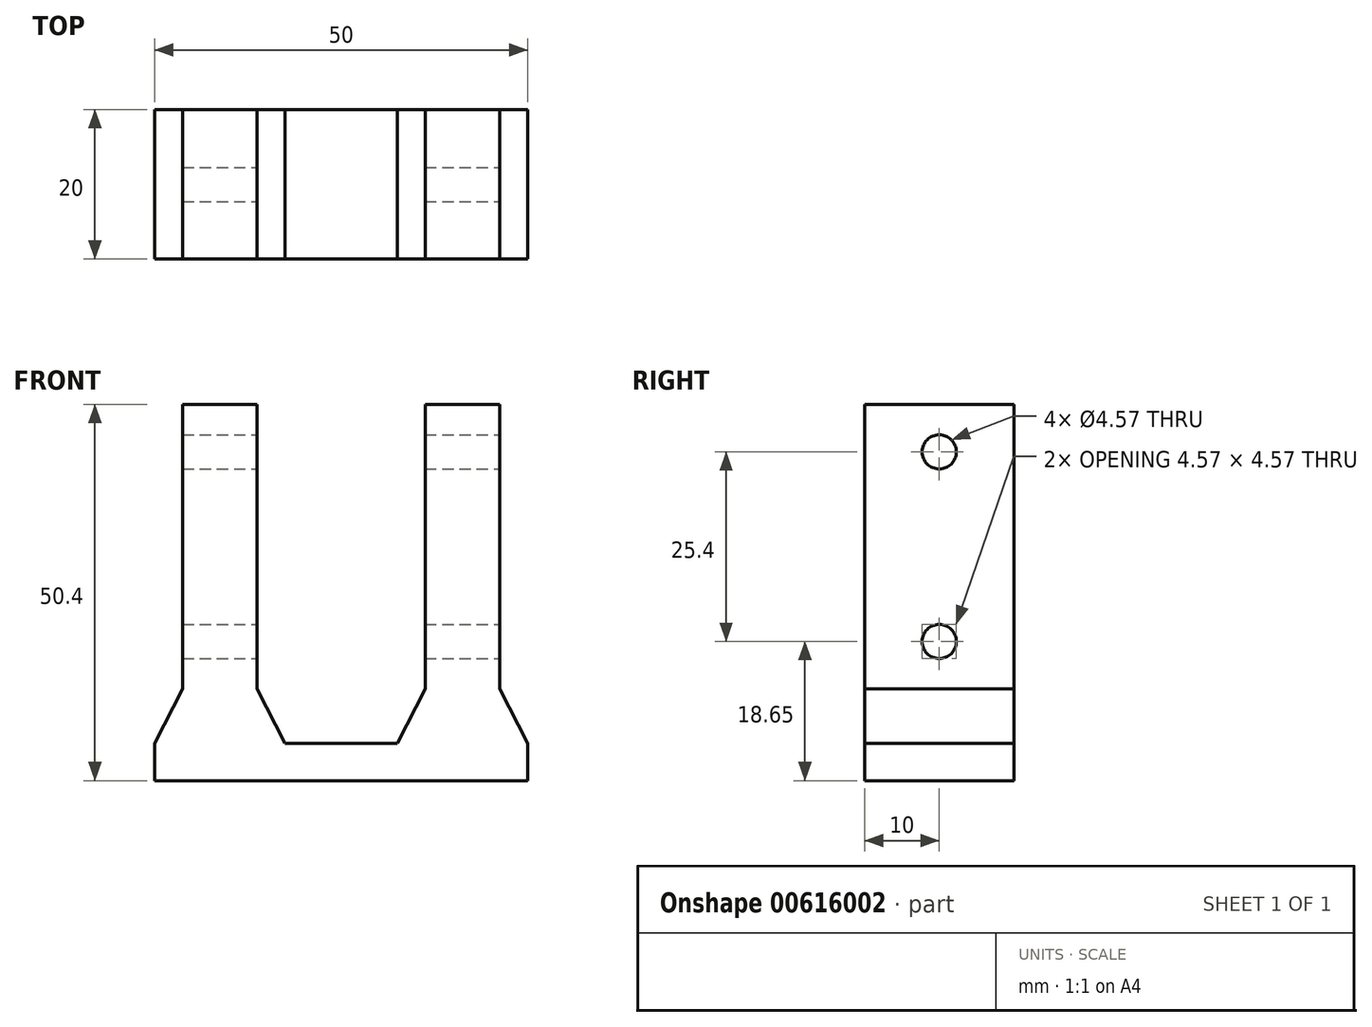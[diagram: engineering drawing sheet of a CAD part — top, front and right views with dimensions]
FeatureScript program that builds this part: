
annotation { "Feature Type Name" : "Feature", "Feature Type Description" : "" }
export const myFeature = defineFeature(function(context is Context, id is Id, definition is map)
    precondition{}
    {
        {
            var Q0;
            Q0=qCreatedBy(makeId("Top.planeOp"),FACE);
            var sketch = newSketch(context, id + "F0", { "sketchPlane" : qUnion([Q0])});
            skLineSegment(sketch, "E0.bottom", {"start": v(25, 10) * mm, "end": v(-25, 10) * mm});
            skLineSegment(sketch, "E0.top", {"start": v(25, -10) * mm, "end": v(-25, -10) * mm});
            skLineSegment(sketch, "E0.left", {"start": v(25, 10) * mm, "end": v(25, -10) * mm});
            skLineSegment(sketch, "E0.right", {"start": v(-25, 10) * mm, "end": v(-25, -10) * mm});
            skPoint(sketch, "E0.middle", {"position": v(0, 0) * mm});
            skSolve(sketch);
        }
        {
            var Q0;
            Q0=makeQuery(id+"F0.imprint","IMPRINT",FACE,{"disambiguationData":[TD([[makeQuery(id+"F0.imprint","IMPRINT",EDGE,{"derivedFrom":sQuery(id+"F0.wireOp",EDGE,"E0.bottom")}),1.0]])]});
            extrude(context, id + "F1", {"entities" : qUnion([Q0]), "depth" : 5 * mm, "offsetDistance" : 25 * mm});
        }
        {
            var Q0;
            Q0=makeQuery(id+"F1.opExtrude","CAP_FACE",FACE,{"disambiguationData":[OSD([sQuery(id+"F0.wireOp",EDGE,"E0.bottom"),sQuery(id+"F0.wireOp",EDGE,"E0.top"),sQuery(id+"F0.wireOp",EDGE,"E0.left"),sQuery(id+"F0.wireOp",EDGE,"E0.right")])],"isStart":false});
            var sketch = newSketch(context, id + "F2", { "sketchPlane" : qUnion([Q0])});
            skLineSegment(sketch, "E1.bottom", {"start": v(25, -10) * mm, "end": v(7.5, -10) * mm});
            skLineSegment(sketch, "E1.top", {"start": v(25, 10) * mm, "end": v(7.5, 10) * mm});
            skLineSegment(sketch, "E1.left", {"start": v(25, -10) * mm, "end": v(25, 10) * mm});
            skLineSegment(sketch, "E1.right", {"start": v(7.5, -10) * mm, "end": v(7.5, 10) * mm});
            skLineSegment(sketch, "E2.bottom", {"start": v(-25, 10) * mm, "end": v(-7.5, 10) * mm});
            skLineSegment(sketch, "E2.top", {"start": v(-25, -10) * mm, "end": v(-7.5, -10) * mm});
            skLineSegment(sketch, "E2.left", {"start": v(-25, 10) * mm, "end": v(-25, -10) * mm});
            skLineSegment(sketch, "E2.right", {"start": v(-7.5, 10) * mm, "end": v(-7.5, -10) * mm});
            skSolve(sketch);
        }
        {
            var Q0;
            Q0=qSketchRegion(id+"F2",true);
            extrude(context, id + "F3", {"entities" : qUnion([Q0]), "operationType" : NewBodyOperationType.ADD, "depth" : 20 * mm, "offsetDistance" : 25 * mm});
        }
        {
            var Q0;
            Q0=makeQuery(id+"F3.opExtrude","CAP_FACE",FACE,{"disambiguationData":[OSD([sQuery(id+"F2.wireOp",EDGE,"E1.bottom"),sQuery(id+"F2.wireOp",EDGE,"E1.top"),sQuery(id+"F2.wireOp",EDGE,"E1.left"),sQuery(id+"F2.wireOp",EDGE,"E1.right")])],"isStart":false});
            var Q1;
            Q1=makeQuery(id+"F3.opExtrude","CAP_FACE",FACE,{"disambiguationData":[OSD([sQuery(id+"F2.wireOp",EDGE,"E2.bottom"),sQuery(id+"F2.wireOp",EDGE,"E2.top"),sQuery(id+"F2.wireOp",EDGE,"E2.left"),sQuery(id+"F2.wireOp",EDGE,"E2.right")])],"isStart":false});
            extrude(context, id + "F4", {"entities" : qUnion([Q0, Q1]), "operationType" : NewBodyOperationType.ADD, "depth" : 1.27 * 20 * mm, "offsetDistance" : 25 * mm});
        }
        {
            var Q0;
            {var subQ0=sQuery(id+"F2.wireOp",EDGE,"E1.left");Q0=makeQuery(id+"F4.boolean.opBoolean","MERGE",FACE,{"derivedFrom":[makeQuery(id+"F3.boolean.opBoolean","MERGE",FACE,{"derivedFrom":[makeQuery(id+"F1.opExtrude","SWEPT_FACE",FACE,{"disambiguationData":[OSD([sQuery(id+"F0.wireOp",EDGE,"E0.left")])]}),makeQuery(id+"F3.opExtrude","SWEPT_FACE",FACE,{"disambiguationData":[OSD([subQ0])]})]}),makeQuery(id+"F4.opExtrude","SWEPT_FACE",FACE,{"disambiguationData":[OSD([subQ0])]})]});}
            var sketch = newSketch(context, id + "F5", { "sketchPlane" : qUnion([Q0])});
            skLineSegment(sketch, "E3", {"start": v(-10, 50.4) * mm, "end": v(10, 37.7) * mm, "construction": true});
            skLineSegment(sketch, "E4", {"start": v(10, 37.7) * mm, "end": v(-10, 37.7) * mm, "construction": true});
            skLineSegment(sketch, "E5", {"start": v(-10, 37.7) * mm, "end": v(10, 50.4) * mm, "construction": true});
            skCircle(sketch, "E6", {"center": v(0, 44.05) * mm, "radius": 2.29 * mm});
            skLineSegment(sketch, "E7", {"start": v(10, 25) * mm, "end": v(-10, 25) * mm, "construction": true});
            skLineSegment(sketch, "E8", {"start": v(-10, 12.3) * mm, "end": v(10, 12.3) * mm, "construction": true});
            skLineSegment(sketch, "E9", {"start": v(-10, 12.3) * mm, "end": v(10, 25) * mm, "construction": true});
            skLineSegment(sketch, "E10", {"start": v(10, 12.3) * mm, "end": v(-10, 25) * mm, "construction": true});
            skCircle(sketch, "E11", {"center": v(0, 18.65) * mm, "radius": 2.29 * mm});
            skSolve(sketch);
        }
        {
            var Q0;
            Q0 = qSketchRegion(id + "F5", true);
            var Q1;
            Q1=sQuery(id+"F5.wireOp",EDGE,"E6");
            var Q2;
            Q2=sQuery(id+"F5.wireOp",EDGE,"UpPk794p-QXIf-7Tcr-FOt5-d0txEuTVeCPj");
            extrude(context, id + "F6", {"entities" : qUnion([Q0]), "operationType" : NewBodyOperationType.REMOVE, "surfaceEntities" : qUnion([Q1, Q2]), "endBound" : BoundingType.THROUGH_ALL, "oppositeDirection" : true, "depth" : 25 * mm, "offsetDistance" : 25 * mm});
        }
        {
            var Q0;
            {var subQ0=sQuery(id+"F2.wireOp",EDGE,"E2.top");var subQ1=sQuery(id+"F2.wireOp",EDGE,"E1.bottom");Q0=makeQuery(id+"F4.boolean.opBoolean","MERGE",FACE,{"derivedFrom":[makeQuery(id+"F3.boolean.opBoolean","MERGE",FACE,{"derivedFrom":[makeQuery(id+"F1.opExtrude","SWEPT_FACE",FACE,{"disambiguationData":[OSD([sQuery(id+"F0.wireOp",EDGE,"E0.top")])]}),makeQuery(id+"F3.opExtrude","SWEPT_FACE",FACE,{"disambiguationData":[OSD([subQ1])]}),makeQuery(id+"F3.opExtrude","SWEPT_FACE",FACE,{"disambiguationData":[OSD([subQ0])]})]}),makeQuery(id+"F4.opExtrude","SWEPT_FACE",FACE,{"disambiguationData":[OSD([subQ1])]}),makeQuery(id+"F4.opExtrude","SWEPT_FACE",FACE,{"disambiguationData":[OSD([subQ0])]})]});}
            var sketch = newSketch(context, id + "F7", { "sketchPlane" : qUnion([Q0])});
            skLineSegment(sketch, "E12", {"start": v(25, 5) * mm, "end": v(-25, 5) * mm, "construction": true});
            skLineSegment(sketch, "E13", {"start": v(-7.5, 5) * mm, "end": v(-25, 5) * mm});
            skLineSegment(sketch, "E14", {"start": v(7.5, 5) * mm, "end": v(25, 5) * mm});
            skLineSegment(sketch, "E15", {"start": v(-25, 5) * mm, "end": v(-21.25, 12.3) * mm});
            skLineSegment(sketch, "E16", {"start": v(-21.25, 12.3) * mm, "end": v(-21.25, 50.4) * mm});
            skPoint(sketch, "E16.endSnap0", {"position": v(-16.25, 50.4) * mm});
            skLineSegment(sketch, "E17", {"start": v(-21.25, 50.4) * mm, "end": v(-11.25, 50.4) * mm});
            skLineSegment(sketch, "E18", {"start": v(-11.25, 50.4) * mm, "end": v(-11.25, 12.3) * mm});
            skLineSegment(sketch, "E19", {"start": v(-11.25, 12.3) * mm, "end": v(-7.5, 5) * mm});
            skLineSegment(sketch, "E20", {"start": v(7.5, 5) * mm, "end": v(11.25, 12.3) * mm});
            skLineSegment(sketch, "E21", {"start": v(11.25, 12.3) * mm, "end": v(11.25, 50.4) * mm});
            skLineSegment(sketch, "E22", {"start": v(11.25, 50.4) * mm, "end": v(21.25, 50.4) * mm});
            skLineSegment(sketch, "E23", {"start": v(21.25, 50.4) * mm, "end": v(21.25, 12.3) * mm});
            skLineSegment(sketch, "E24", {"start": v(21.25, 12.3) * mm, "end": v(25, 5) * mm});
            skSolve(sketch);
        }
        {
            var Q0;
            {var subQ0=sQuery(id+"F7.wireOp",EDGE,"E15");Q0=makeQuery(id+"F7.imprint","IMPRINT",FACE,{"disambiguationData":[TD([[makeQuery(id+"F7.imprint","IMPRINT",EDGE,{"derivedFrom":subQ0}),1.0]])]});}
            var Q1;
            {var subQ0=sQuery(id+"F7.wireOp",EDGE,"E18");Q1=makeQuery(id+"F7.imprint","IMPRINT",FACE,{"disambiguationData":[TD([[makeQuery(id+"F7.imprint","IMPRINT",EDGE,{"derivedFrom":subQ0}),1.0]])]});}
            var Q2;
            Q2=makeQuery(id+"F7.imprint","IMPRINT",FACE,{"disambiguationData":[TD([[makeQuery(id+"F7.imprint","IMPRINT",EDGE,{"derivedFrom":sQuery(id+"F7.wireOp",EDGE,"E20")}),1.0]])]});
            var Q3;
            {var subQ0=sQuery(id+"F7.wireOp",EDGE,"E23");Q3=makeQuery(id+"F7.imprint","IMPRINT",FACE,{"disambiguationData":[TD([[makeQuery(id+"F7.imprint","IMPRINT",EDGE,{"derivedFrom":subQ0}),1.0]])]});}
            extrude(context, id + "F8", {"entities" : qUnion([Q0, Q1, Q2, Q3]), "operationType" : NewBodyOperationType.REMOVE, "endBound" : BoundingType.THROUGH_ALL, "oppositeDirection" : true, "depth" : 25 * mm, "offsetDistance" : 25 * mm});
        }
    });
